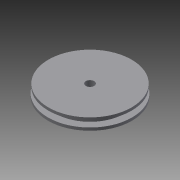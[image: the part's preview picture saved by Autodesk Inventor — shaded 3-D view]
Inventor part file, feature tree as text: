
AUTODESK INVENTOR PART (.ipt)
format: ipt  version: 2015 (Build 190159000, 159)  size: 94,208 bytes
history: native  units: mm
features: extrude x4, sketch x4
ambient origin geometry x8: Origin, YZ Plane, XZ Plane, XY Plane, X Axis, Y Axis, Z Axis, Center Point
bodies: Solid1 (feature_tree)
feature tree (8):
  extrude  "Extrusion1"  Depth=1.0mm TaperAngle=0.0deg
  extrude  "Extrusion2"  Depth=2.0mm TaperAngle=0.0deg
  extrude  "Extrusion3"  Depth=3.0mm
  extrude  "Extrusion4"  [1 undecoded]
  sketch  "Sketch1"  dims[d0=30.0mm d1=1.0mm d2=0.0mm]
  sketch  "Sketch2"  dims[d3=25.0mm d4=2.0mm d5=0.0mm]
  sketch  "Sketch3"  dims[d6=1.0mm d7=0.0mm d8=3.0mm]
  sketch  "Sketch4"  dims[d9=5.0mm d10=0.0mm]
note: 1 required parameter value undecoded (feature->parameter linkage not recoverable at this tier; creation-order binding heuristic only, values carry confidence <= 0.55)
